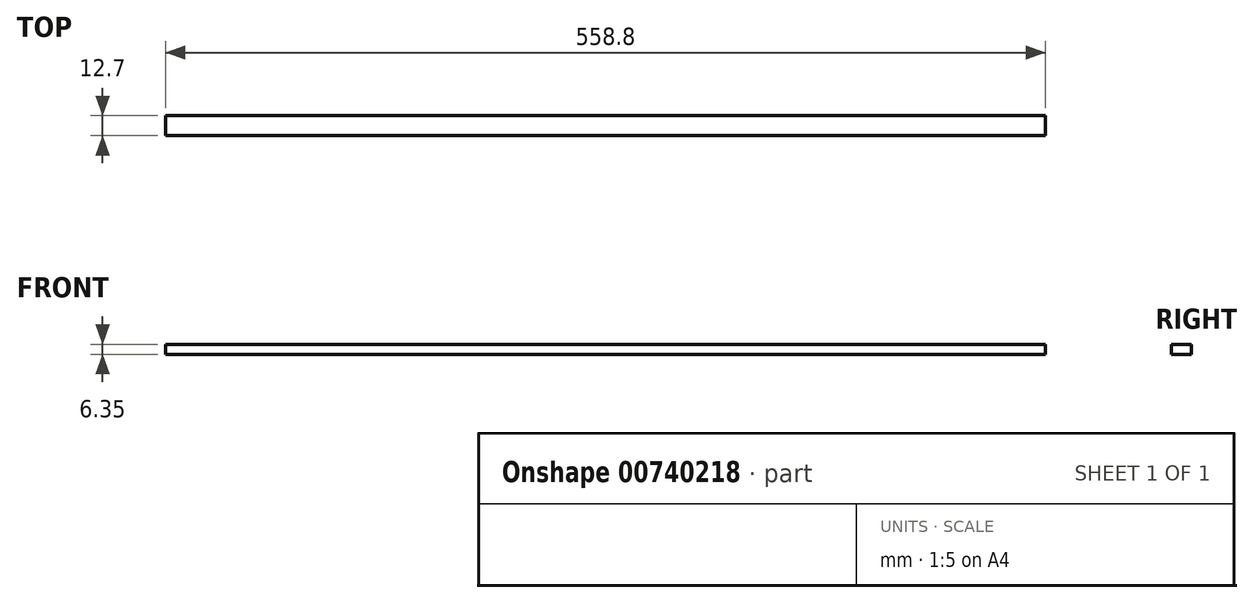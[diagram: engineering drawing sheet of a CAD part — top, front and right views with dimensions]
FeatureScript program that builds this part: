
annotation { "Feature Type Name" : "Feature", "Feature Type Description" : "" }
export const myFeature = defineFeature(function(context is Context, id is Id, definition is map)
    precondition{}
    {
        {
            var Q0;
            Q0=qCreatedBy(makeId("Top.planeOp"),FACE);
            var sketch = newSketch(context, id + "F0", { "sketchPlane" : qUnion([Q0])});
            skLineSegment(sketch, "E0.bottom", {"start": v(0, 0) * mm, "end": v(558.8, 0) * mm});
            skLineSegment(sketch, "E0.top", {"start": v(0, -12.7) * mm, "end": v(558.8, -12.7) * mm});
            skLineSegment(sketch, "E0.left", {"start": v(0, 0) * mm, "end": v(0, -12.7) * mm});
            skLineSegment(sketch, "E0.right", {"start": v(558.8, 0) * mm, "end": v(558.8, -12.7) * mm});
            skSolve(sketch);
        }
        {
            var Q0;
            Q0=makeQuery(id+"F0.imprint","IMPRINT",FACE,{"disambiguationData":[TD([[makeQuery(id+"F0.imprint","IMPRINT",EDGE,{"derivedFrom":sQuery(id+"F0.wireOp",EDGE,"E0.bottom")}),-1.0]])]});
            extrude(context, id + "F1", {"entities" : qUnion([Q0]), "depth" : 6.35 * mm, "offsetDistance" : 25.4 * mm});
        }
    });
